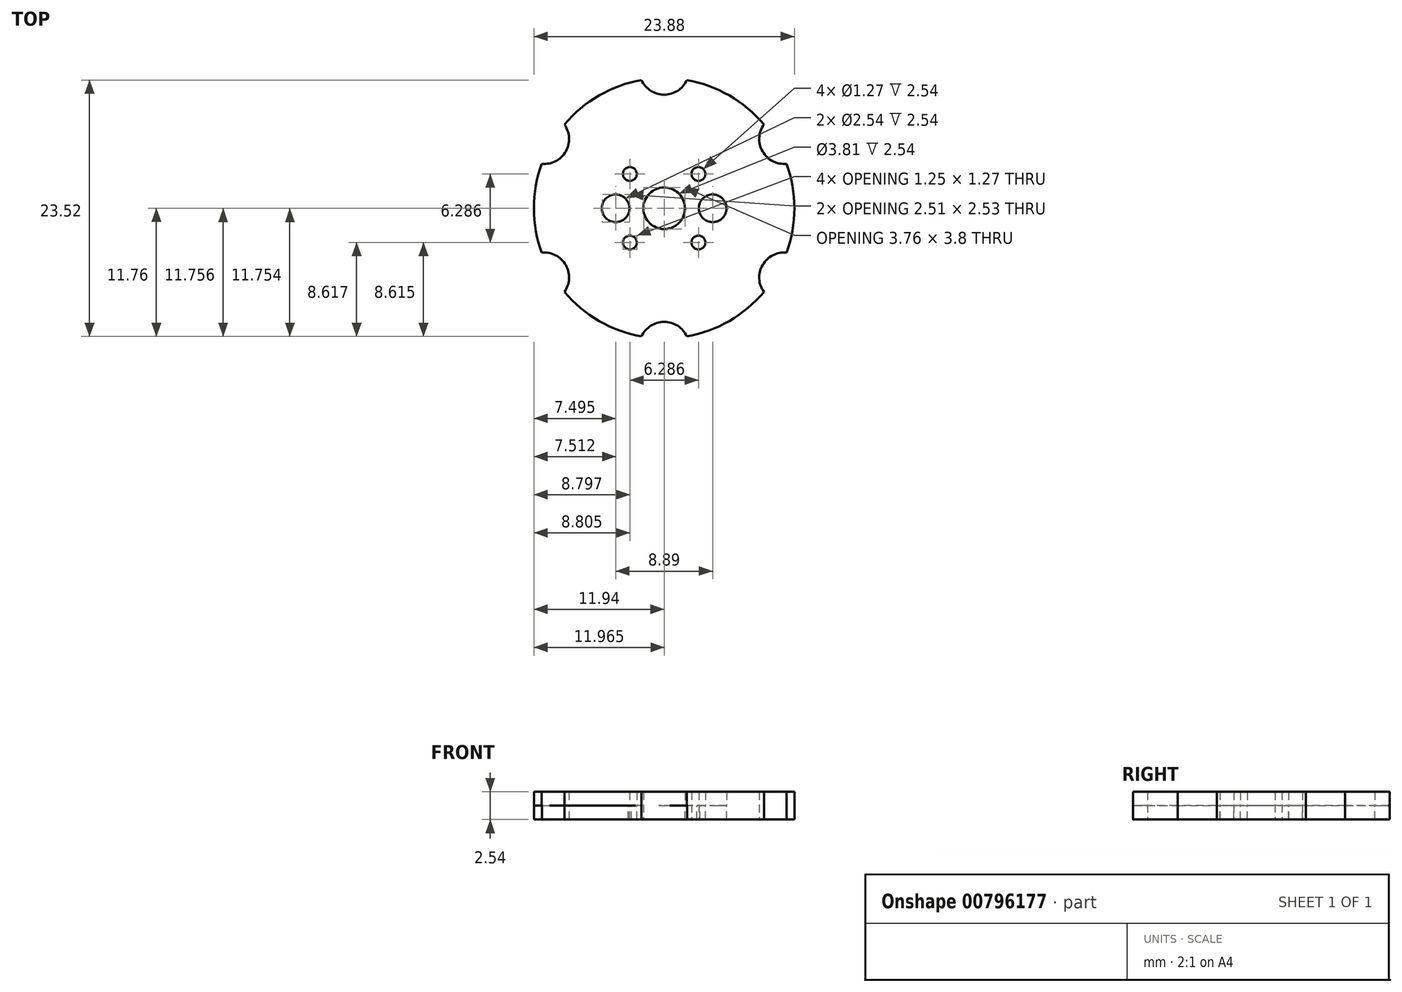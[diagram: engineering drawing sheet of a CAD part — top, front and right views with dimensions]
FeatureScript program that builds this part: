
annotation { "Feature Type Name" : "Feature", "Feature Type Description" : "" }
export const myFeature = defineFeature(function(context is Context, id is Id, definition is map)
    precondition{}
    {
        {
            var Q0;
            Q0=qCreatedBy(makeId("Top.planeOp"),FACE);
            var sketch = newSketch(context, id + "F0", { "sketchPlane" : qUnion([Q0])});
            skPoint(sketch, "E0.center", {"position": v(0, 0) * mm});
            skArc(sketch, "E1", {"start": v(-11.22, 4.07) * mm, "mid": v(-11.94, 0) * mm, "end": v(-11.22, -4.07) * mm});
            skArc(sketch, "E2.trimOffspring", {"start": v(-9.14, -7.68) * mm, "mid": v(-5.97, -10.34) * mm, "end": v(-2.08, -11.76) * mm});
            skArc(sketch, "E3.trimOffspring", {"start": v(2.08, -11.76) * mm, "mid": v(5.97, -10.34) * mm, "end": v(9.14, -7.68) * mm});
            skArc(sketch, "E4.trimOffspring", {"start": v(11.22, -4.07) * mm, "mid": v(11.94, 0) * mm, "end": v(11.22, 4.07) * mm});
            skArc(sketch, "E5.trimOffspring", {"start": v(9.14, 7.68) * mm, "mid": v(5.97, 10.34) * mm, "end": v(2.08, 11.76) * mm});
            skArc(sketch, "E6.trimOffspring", {"start": v(-2.08, 11.76) * mm, "mid": v(-5.97, 10.34) * mm, "end": v(-9.14, 7.68) * mm});
            skArc(sketch, "E7", {"start": v(-11.22, 4.07) * mm, "mid": v(-9.02, 5.2) * mm, "end": v(-9.14, 7.68) * mm});
            skArc(sketch, "E8", {"start": v(-2.08, 11.76) * mm, "mid": v(0, 10.41) * mm, "end": v(2.08, 11.76) * mm});
            skArc(sketch, "E9", {"start": v(9.14, 7.68) * mm, "mid": v(9.02, 5.2) * mm, "end": v(11.22, 4.07) * mm});
            skArc(sketch, "E10", {"start": v(11.22, -4.07) * mm, "mid": v(9.02, -5.2) * mm, "end": v(9.14, -7.68) * mm});
            skArc(sketch, "E11", {"start": v(-9.14, -7.68) * mm, "mid": v(-9.02, -5.2) * mm, "end": v(-11.22, -4.07) * mm});
            skArc(sketch, "E12.trimOffspring", {"start": v(2.08, -11.76) * mm, "mid": v(0, -10.41) * mm, "end": v(-2.08, -11.76) * mm});
            skCircle(sketch, "E13", {"center": v(-4.45, 0) * mm, "radius": 1.27 * mm});
            skCircle(sketch, "E14", {"center": v(4.44, 0) * mm, "radius": 1.27 * mm});
            skCircle(sketch, "E15", {"center": v(-3.14, 3.14) * mm, "radius": 0.64 * mm});
            skCircle(sketch, "E16.1.0", {"center": v(-3.14, -3.14) * mm, "radius": 0.64 * mm});
            skCircle(sketch, "E16.2.0", {"center": v(3.14, -3.14) * mm, "radius": 0.64 * mm});
            skCircle(sketch, "E16.3.0", {"center": v(3.14, 3.14) * mm, "radius": 0.64 * mm});
            skCircle(sketch, "E17", {"center": v(0, 0) * mm, "radius": 1.9 * mm});
            skSolve(sketch);
        }
        {
            var Q0;
            Q0=makeQuery(id+"F0.imprint","IMPRINT",FACE,{"disambiguationData":[TD([[makeQuery(id+"F0.imprint","IMPRINT",EDGE,{"derivedFrom":sQuery(id+"F0.wireOp",EDGE,"E1")}),1.0]])]});
            extrude(context, id + "F1", {"entities" : qUnion([Q0]), "depth" : 1.27 * mm, "offsetDistance" : 25.4 * mm});
        }
        {
            var Q0;
            Q0=makeQuery(id+"F1.opExtrude","CAP_FACE",FACE,{"disambiguationData":[OSD([sQuery(id+"F0.wireOp",EDGE,"E1"),sQuery(id+"F0.wireOp",EDGE,"E2.trimOffspring"),sQuery(id+"F0.wireOp",EDGE,"E3.trimOffspring"),sQuery(id+"F0.wireOp",EDGE,"E4.trimOffspring"),sQuery(id+"F0.wireOp",EDGE,"E5.trimOffspring"),sQuery(id+"F0.wireOp",EDGE,"E6.trimOffspring"),sQuery(id+"F0.wireOp",EDGE,"E7"),sQuery(id+"F0.wireOp",EDGE,"E8"),sQuery(id+"F0.wireOp",EDGE,"E9"),sQuery(id+"F0.wireOp",EDGE,"E10"),sQuery(id+"F0.wireOp",EDGE,"E11"),sQuery(id+"F0.wireOp",EDGE,"E12.trimOffspring"),sQuery(id+"F0.wireOp",EDGE,"E13"),sQuery(id+"F0.wireOp",EDGE,"E14"),sQuery(id+"F0.wireOp",EDGE,"E15"),sQuery(id+"F0.wireOp",EDGE,"E16.1.0"),sQuery(id+"F0.wireOp",EDGE,"E16.2.0"),sQuery(id+"F0.wireOp",EDGE,"E16.3.0"),sQuery(id+"F0.wireOp",EDGE,"E17")])],"isStart":true});
            var sketch = newSketch(context, id + "F2", { "sketchPlane" : qUnion([Q0])});
            skPoint(sketch, "E18.center", {"position": v(0.01, 0) * mm});
            skArc(sketch, "E19", {"start": v(-11.2, 4.08) * mm, "mid": v(-11.93, 0) * mm, "end": v(-11.2, -4.07) * mm});
            skArc(sketch, "E20.trimOffspring", {"start": v(-9.13, -7.68) * mm, "mid": v(-5.96, -10.34) * mm, "end": v(-2.07, -11.75) * mm});
            skArc(sketch, "E21.trimOffspring", {"start": v(2.1, -11.75) * mm, "mid": v(5.98, -10.34) * mm, "end": v(9.15, -7.68) * mm});
            skArc(sketch, "E22.trimOffspring", {"start": v(11.23, -4.07) * mm, "mid": v(11.95, 0) * mm, "end": v(11.23, 4.08) * mm});
            skArc(sketch, "E23.trimOffspring", {"start": v(9.15, 7.68) * mm, "mid": v(5.98, 10.34) * mm, "end": v(2.1, 11.76) * mm});
            skArc(sketch, "E24.trimOffspring", {"start": v(-2.07, 11.76) * mm, "mid": v(-5.96, 10.34) * mm, "end": v(-9.13, 7.68) * mm});
            skArc(sketch, "E25", {"start": v(-11.2, 4.08) * mm, "mid": v(-9, 5.2) * mm, "end": v(-9.13, 7.68) * mm});
            skArc(sketch, "E26", {"start": v(-2.07, 11.76) * mm, "mid": v(0.01, 10.42) * mm, "end": v(2.1, 11.76) * mm});
            skArc(sketch, "E27", {"start": v(9.15, 7.68) * mm, "mid": v(9.03, 5.2) * mm, "end": v(11.23, 4.08) * mm});
            skArc(sketch, "E28", {"start": v(11.23, -4.07) * mm, "mid": v(9.03, -5.2) * mm, "end": v(9.15, -7.68) * mm});
            skArc(sketch, "E29", {"start": v(-9.13, -7.68) * mm, "mid": v(-9, -5.2) * mm, "end": v(-11.2, -4.07) * mm});
            skArc(sketch, "E30.trimOffspring", {"start": v(2.1, -11.75) * mm, "mid": v(0.01, -10.41) * mm, "end": v(-2.07, -11.75) * mm});
            skCircle(sketch, "E31", {"center": v(-4.43, 0) * mm, "radius": 1.27 * mm});
            skCircle(sketch, "E32", {"center": v(4.46, 0) * mm, "radius": 1.27 * mm});
            skCircle(sketch, "E33", {"center": v(-3.13, 3.15) * mm, "radius": 0.64 * mm});
            skCircle(sketch, "E34.1.0", {"center": v(-3.13, -3.14) * mm, "radius": 0.64 * mm});
            skCircle(sketch, "E34.2.0", {"center": v(3.15, -3.14) * mm, "radius": 0.64 * mm});
            skCircle(sketch, "E34.3.0", {"center": v(3.15, 3.15) * mm, "radius": 0.64 * mm});
            skCircle(sketch, "E35", {"center": v(0.01, 0) * mm, "radius": 1.9 * mm});
            skSolve(sketch);
        }
        {
            var Q0;
            {var subQ47=sQuery(id+"F2.wireOp",EDGE,"E29");Q0=makeQuery(id+"F2.imprint","IMPRINT",FACE,{"disambiguationData":[TD([[makeQuery(id+"F2.imprint","IMPRINT",EDGE,{"derivedFrom":subQ47}),-1.0]])]});}
            extrude(context, id + "F3", {"entities" : qUnion([Q0]), "operationType" : NewBodyOperationType.ADD, "depth" : 1.27 * mm, "offsetDistance" : 25.4 * mm});
        }
    });
